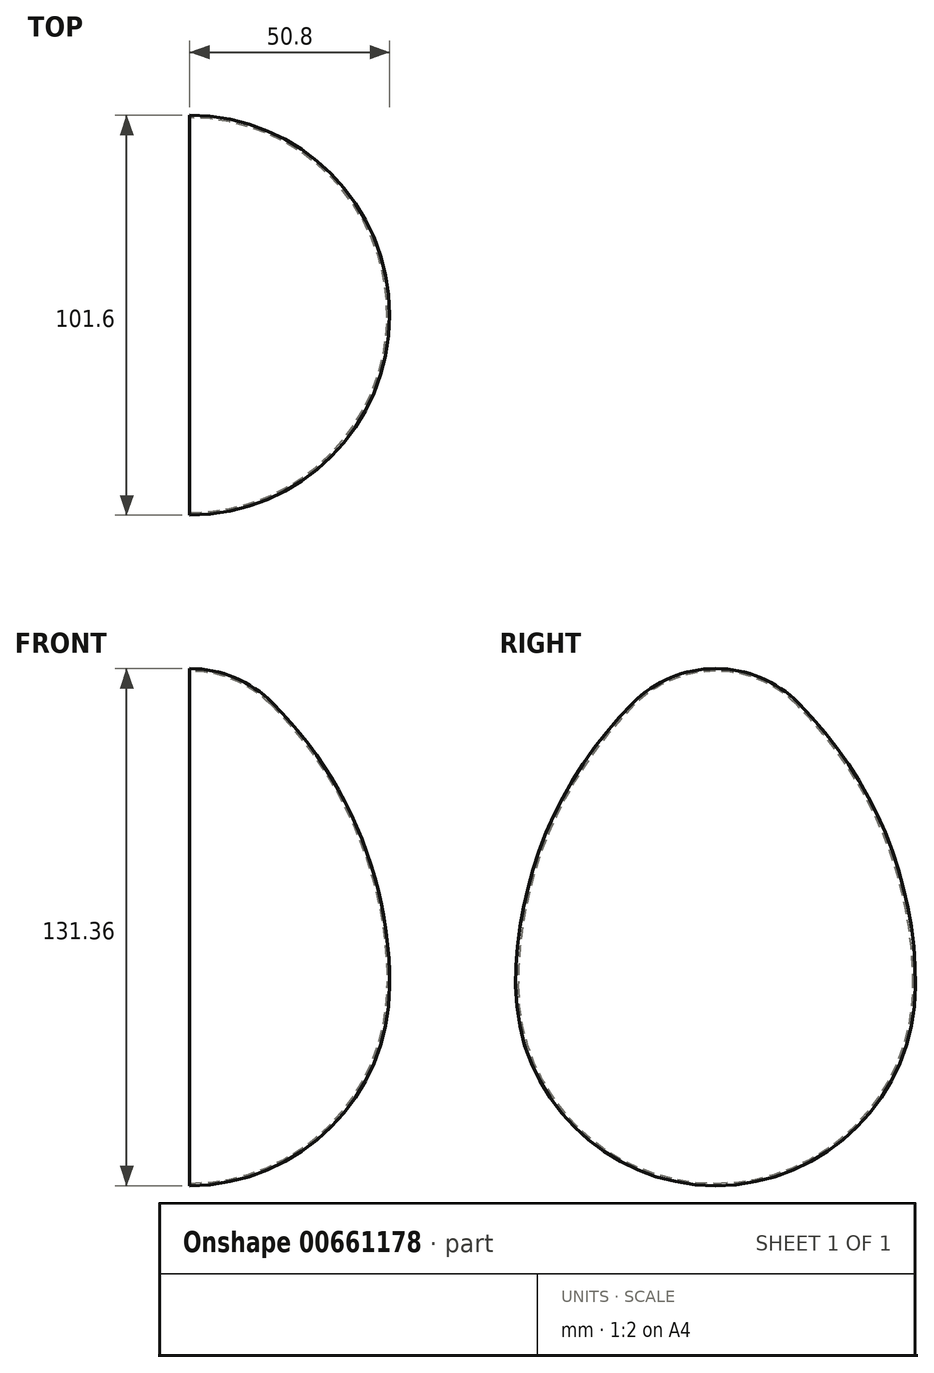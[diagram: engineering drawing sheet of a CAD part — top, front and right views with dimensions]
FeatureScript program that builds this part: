
annotation { "Feature Type Name" : "Feature", "Feature Type Description" : "" }
export const myFeature = defineFeature(function(context is Context, id is Id, definition is map)
    precondition{}
    {
        {
            var Q0;
            Q0=qCreatedBy(makeId("Front.planeOp"),FACE);
            var sketch = newSketch(context, id + "F0", { "sketchPlane" : qUnion([Q0])});
            skArc(sketch, "E0", {"start": v(0, -50.8) * mm, "mid": v(35.92, -35.92) * mm, "end": v(50.8, 0) * mm});
            skLineSegment(sketch, "E1", {"start": v(0, 0) * mm, "end": v(0, -50.8) * mm});
            skPoint(sketch, "E2", {"position": v(0, -50.8) * mm});
            skPoint(sketch, "E3", {"position": v(50.8, 0) * mm});
            skPoint(sketch, "E4", {"position": v(0, 50.8) * mm});
            skArc(sketch, "E5", {"start": v(50.8, 0) * mm, "mid": v(43.07, 38.88) * mm, "end": v(21.04, 71.84) * mm});
            skArc(sketch, "E6", {"start": v(21.04, 71.84) * mm, "mid": v(11.39, 78.3) * mm, "end": v(0, 80.56) * mm});
            skLineSegment(sketch, "E7", {"start": v(0, 80.56) * mm, "end": v(0, 50.8) * mm});
            skLineSegment(sketch, "E8", {"start": v(0, 50.8) * mm, "end": v(0, 0) * mm});
            skPoint(sketch, "E9", {"position": v(0, 80.56) * mm});
            skPoint(sketch, "E10", {"position": v(21.04, 71.84) * mm});
            skArc(sketch, "E11", {"start": v(41.28, 0) * mm, "mid": v(38.1, 3.18) * mm, "end": v(34.93, 0) * mm});
            skArc(sketch, "E12", {"start": v(0, -41.28) * mm, "mid": v(29.19, -29.19) * mm, "end": v(41.28, 0) * mm});
            skArc(sketch, "E13", {"start": v(0, -34.93) * mm, "mid": v(24.7, -24.7) * mm, "end": v(34.93, 0) * mm});
            skArc(sketch, "E14.MirrorCS", {"start": v(-21.04, 71.84) * mm, "mid": v(-11.39, 78.3) * mm, "end": v(0, 80.56) * mm});
            skArc(sketch, "E15.MirrorCS", {"start": v(-50.8, 0) * mm, "mid": v(-43.07, 38.88) * mm, "end": v(-21.04, 71.84) * mm});
            skArc(sketch, "E16.MirrorCS", {"start": v(0, -50.8) * mm, "mid": v(-35.92, -35.92) * mm, "end": v(-50.8, 0) * mm});
            skArc(sketch, "E17.MirrorCS", {"start": v(0, -34.92) * mm, "mid": v(-24.7, -24.7) * mm, "end": v(-34.92, 0) * mm});
            skArc(sketch, "E18.MirrorCS", {"start": v(0, -41.27) * mm, "mid": v(-29.19, -29.19) * mm, "end": v(-41.27, 0) * mm});
            skArc(sketch, "E19.MirrorCS", {"start": v(-41.27, 0) * mm, "mid": v(-38.1, 3.17) * mm, "end": v(-34.92, 0) * mm});
            skCircle(sketch, "E20", {"center": v(0, 0) * mm, "radius": 6.35 * mm});
            skLineSegment(sketch, "E21", {"start": v(0, -50.8) * mm, "end": v(0, -41.27) * mm});
            skLineSegment(sketch, "E22", {"start": v(0, -34.92) * mm, "end": v(0, -6.35) * mm});
            skLineSegment(sketch, "E23", {"start": v(0, 6.35) * mm, "end": v(0, 80.56) * mm});
            skSolve(sketch);
        }
        {
            var Q0;
            Q0=qCreatedBy(makeId("Right.planeOp"),FACE);
            var sketch = newSketch(context, id + "F1", { "sketchPlane" : qUnion([Q0])});
            skArc(sketch, "E24", {"start": v(-50.8, 0) * mm, "mid": v(0, -50.8) * mm, "end": v(50.8, 0) * mm});
            skLineSegment(sketch, "E25", {"start": v(0, 0) * mm, "end": v(-50.8, 0) * mm});
            skLineSegment(sketch, "E26", {"start": v(0, 0) * mm, "end": v(50.8, 0) * mm});
            skPoint(sketch, "E27", {"position": v(0, -50.8) * mm});
            skPoint(sketch, "E28", {"position": v(0, 50.8) * mm});
            skPoint(sketch, "E29", {"position": v(-50.8, 0) * mm});
            skPoint(sketch, "E30", {"position": v(50.8, 0) * mm});
            skArc(sketch, "E31", {"start": v(50.8, 0) * mm, "mid": v(43.07, 38.88) * mm, "end": v(21.04, 71.84) * mm});
            skArc(sketch, "E32", {"start": v(-21.04, 71.84) * mm, "mid": v(-43.07, 38.88) * mm, "end": v(-50.8, 0) * mm});
            skArc(sketch, "E33", {"start": v(0, 80.56) * mm, "mid": v(-11.39, 78.3) * mm, "end": v(-21.04, 71.84) * mm});
            skArc(sketch, "E34", {"start": v(21.04, 71.84) * mm, "mid": v(11.39, 78.3) * mm, "end": v(0, 80.56) * mm});
            skLineSegment(sketch, "E35", {"start": v(0, 80.56) * mm, "end": v(0, -50.8) * mm});
            skSolve(sketch);
        }
        {
            var Q0;
            {var subQ0=sQuery(id+"F1.wireOp",EDGE,"E26");Q0=makeQuery(id+"F1.imprint","IMPRINT",FACE,{"disambiguationData":[TD([[makeQuery(id+"F1.imprint","IMPRINT",EDGE,{"derivedFrom":subQ0}),1.0]])]});}
            var Q1;
            {var subQ0=sQuery(id+"F1.wireOp",EDGE,"E26");Q1=makeQuery(id+"F1.imprint","IMPRINT",FACE,{"disambiguationData":[TD([[makeQuery(id+"F1.imprint","IMPRINT",EDGE,{"derivedFrom":subQ0}),-1.0]])]});}
            var Q2;
            Q2=sQuery(id+"F1.wireOp",EDGE,"E35");
            revolve(context, id + "F2", {"entities" : qUnion([Q0, Q1]), "axis" : qUnion([Q2]), "revolveType" : RevolveType.ONE_DIRECTION, "angle" : 180 * degree});
        }
        {
            var Q0;
            Q0=makeQuery(id+"F2.opRevolve","CAP_FACE",FACE,{"disambiguationData":[OSD([sQuery(id+"F1.wireOp",EDGE,"E24"),sQuery(id+"F1.wireOp",EDGE,"E31"),sQuery(id+"F1.wireOp",EDGE,"E34"),sQuery(id+"F1.wireOp",EDGE,"E35")])],"isStart":false});
            shell(context, id + "F3", {"entities" : qUnion([Q0]), "thickness" : 0.64 * mm});
        }
    });
